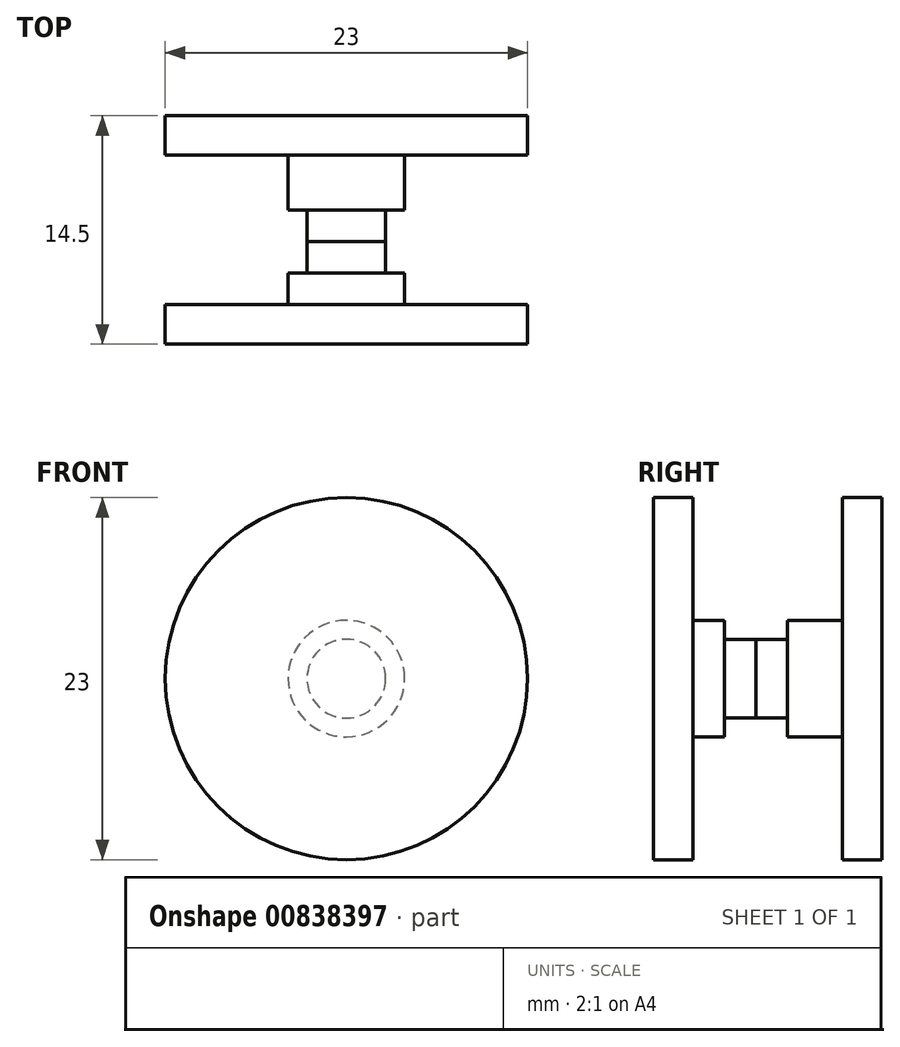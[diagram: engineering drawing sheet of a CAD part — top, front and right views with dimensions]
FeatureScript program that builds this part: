
annotation { "Feature Type Name" : "Feature", "Feature Type Description" : "" }
export const myFeature = defineFeature(function(context is Context, id is Id, definition is map)
    precondition{}
    {
        {
            var Q0;
            Q0=qCreatedBy(makeId("Top.planeOp"),FACE);
            var sketch = newSketch(context, id + "F0", { "sketchPlane" : qUnion([Q0])});
            skLineSegment(sketch, "E0", {"start": v(6.5, 1.25) * mm, "end": v(5, 1.25) * mm});
            skLineSegment(sketch, "E1", {"start": v(5, 1.25) * mm, "end": v(5, 3.25) * mm, "construction": true});
            skLineSegment(sketch, "E2", {"start": v(5, 3.25) * mm, "end": v(6.5, 3.25) * mm, "construction": true});
            skLineSegment(sketch, "E3", {"start": v(6.5, 3.25) * mm, "end": v(6.5, 3.75) * mm, "construction": true});
            skLineSegment(sketch, "E4", {"start": v(6.5, 3.75) * mm, "end": v(8, 3.75) * mm, "construction": true});
            skLineSegment(sketch, "E5", {"start": v(8, 3.75) * mm, "end": v(8, 3.25) * mm, "construction": true});
            skLineSegment(sketch, "E6", {"start": v(8, 3.25) * mm, "end": v(10, 3.25) * mm, "construction": true});
            skLineSegment(sketch, "E7", {"start": v(10, 3.25) * mm, "end": v(10, 3.75) * mm, "construction": true});
            skLineSegment(sketch, "E8", {"start": v(10, 3.75) * mm, "end": v(11.35, 3.75) * mm, "construction": true});
            skLineSegment(sketch, "E9", {"start": v(11.35, 3.75) * mm, "end": v(11.35, 3.25) * mm, "construction": true});
            skLineSegment(sketch, "E10", {"start": v(11.35, 3.25) * mm, "end": v(11.85, 3.25) * mm, "construction": true});
            skLineSegment(sketch, "E11", {"start": v(11.85, 3.25) * mm, "end": v(11.85, 3.75) * mm, "construction": true});
            skLineSegment(sketch, "E12", {"start": v(11.85, 3.75) * mm, "end": v(42, 3.75) * mm, "construction": true});
            skLineSegment(sketch, "E13", {"start": v(42, 3.75) * mm, "end": v(42, -3.75) * mm, "construction": true});
            skLineSegment(sketch, "E14", {"start": v(42, -3.75) * mm, "end": v(11.85, -3.75) * mm, "construction": true});
            skLineSegment(sketch, "E15", {"start": v(11.85, -3.75) * mm, "end": v(11.85, -3.25) * mm, "construction": true});
            skLineSegment(sketch, "E16", {"start": v(11.85, -3.25) * mm, "end": v(11.35, -3.25) * mm, "construction": true});
            skLineSegment(sketch, "E17", {"start": v(11.35, -3.25) * mm, "end": v(11.35, -3.75) * mm, "construction": true});
            skLineSegment(sketch, "E18", {"start": v(10, -3.75) * mm, "end": v(10, -3.25) * mm, "construction": true});
            skLineSegment(sketch, "E19", {"start": v(10, -3.25) * mm, "end": v(8, -3.25) * mm, "construction": true});
            skLineSegment(sketch, "E20", {"start": v(8, -3.25) * mm, "end": v(8, -3.75) * mm, "construction": true});
            skLineSegment(sketch, "E21", {"start": v(8, -3.75) * mm, "end": v(6.5, -3.75) * mm, "construction": true});
            skLineSegment(sketch, "E22", {"start": v(6.5, -3.75) * mm, "end": v(6.5, 1.25) * mm, "construction": true});
            skLineSegment(sketch, "E23", {"start": v(10, -3.75) * mm, "end": v(11.35, -3.75) * mm, "construction": true});
            skLineSegment(sketch, "E24", {"start": v(0, -13.74) * mm, "end": v(0, 16.03) * mm, "construction": true});
            skLineSegment(sketch, "E25.bottom", {"start": v(0, 1.25) * mm, "end": v(2.5, 1.25) * mm});
            skLineSegment(sketch, "E25.top", {"start": v(0, -2.75) * mm, "end": v(2.5, -2.75) * mm});
            skLineSegment(sketch, "E25.left", {"start": v(0, 1.25) * mm, "end": v(0, -2.75) * mm});
            skLineSegment(sketch, "E25.right", {"start": v(6.5, 1.25) * mm, "end": v(6.5, -2.75) * mm});
            skLineSegment(sketch, "E26", {"start": v(2.5, 1.25) * mm, "end": v(2.5, -2.75) * mm});
            skLineSegment(sketch, "E27", {"start": v(3.7, 1.25) * mm, "end": v(3.7, -2.75) * mm, "construction": true});
            skLineSegment(sketch, "E28", {"start": v(0, -0.75) * mm, "end": v(2.5, -0.75) * mm});
            skLineSegment(sketch, "E29", {"start": v(2.5, -0.75) * mm, "end": v(2.5, 1.25) * mm});
            skLineSegment(sketch, "E30", {"start": v(3.7, 4.75) * mm, "end": v(11.5, 4.75) * mm});
            skLineSegment(sketch, "E31", {"start": v(11.5, 4.75) * mm, "end": v(11.5, 7.25) * mm});
            skLineSegment(sketch, "E32", {"start": v(11.5, 7.25) * mm, "end": v(0, 7.25) * mm});
            skLineSegment(sketch, "E33", {"start": v(0, 7.25) * mm, "end": v(0, -0.75) * mm});
            skLineSegment(sketch, "E34", {"start": v(3.7, 4.75) * mm, "end": v(3.7, 1.25) * mm});
            skLineSegment(sketch, "E35", {"start": v(3.7, -2.75) * mm, "end": v(3.7, -4.75) * mm});
            skLineSegment(sketch, "E36", {"start": v(3.7, -4.75) * mm, "end": v(11.5, -4.75) * mm});
            skLineSegment(sketch, "E37", {"start": v(11.5, -4.75) * mm, "end": v(11.5, -7.25) * mm});
            skLineSegment(sketch, "E38", {"start": v(11.5, -7.25) * mm, "end": v(0, -7.25) * mm});
            skLineSegment(sketch, "E39", {"start": v(0, -7.25) * mm, "end": v(0, -0.75) * mm});
            skLineSegment(sketch, "E40", {"start": v(3.7, 1.25) * mm, "end": v(6.5, 1.25) * mm, "construction": true});
            skLineSegment(sketch, "E41", {"start": v(2.5, 1.25) * mm, "end": v(3.7, 1.25) * mm});
            skLineSegment(sketch, "E42", {"start": v(3.7, -2.75) * mm, "end": v(6.5, -2.75) * mm, "construction": true});
            skLineSegment(sketch, "E43", {"start": v(2.5, -2.75) * mm, "end": v(3.7, -2.75) * mm});
            skSolve(sketch);
        }
        {
            var Q0;
            {var subQ4=sQuery(id+"F0.wireOp",EDGE,"E28");Q0=makeQuery(id+"F0.imprint","IMPRINT",FACE,{"disambiguationData":[TD([[makeQuery(id+"F0.imprint","IMPRINT",EDGE,{"derivedFrom":subQ4}),1.0]])]});}
            var Q1;
            Q1=makeQuery(id+"F0.imprint","IMPRINT",FACE,{"disambiguationData":[TD([[makeQuery(id+"F0.imprint","IMPRINT",EDGE,{"derivedFrom":sQuery(id+"F0.wireOp",EDGE,"E30")}),1.0]])]});
            var Q2;
            Q2=sQuery(id+"F0.wireOp",EDGE,"E24");
            revolve(context, id + "F1", {"surfaceOperationType" : NewSurfaceOperationType.NEW, "entities" : qUnion([Q0, Q1]), "axis" : qUnion([Q2]), "revolveType" : RevolveType.FULL});
        }
        {
            var Q0;
            {var subQ3=sQuery(id+"F0.wireOp",EDGE,"E26");Q0=makeQuery(id+"F0.imprint","IMPRINT",FACE,{"disambiguationData":[TD([[makeQuery(id+"F0.imprint","IMPRINT",EDGE,{"derivedFrom":subQ3}),-1.0]])]});}
            var Q1;
            {var subQ2=sQuery(id+"F0.wireOp",EDGE,"E35");Q1=makeQuery(id+"F0.imprint","IMPRINT",FACE,{"disambiguationData":[TD([[makeQuery(id+"F0.imprint","IMPRINT",EDGE,{"derivedFrom":subQ2}),-1.0]])]});}
            var Q2;
            Q2=sQuery(id+"F0.wireOp",EDGE,"E24");
            revolve(context, id + "F2", {"surfaceOperationType" : NewSurfaceOperationType.NEW, "entities" : qUnion([Q0, Q1]), "axis" : qUnion([Q2]), "revolveType" : RevolveType.FULL});
        }
    });
